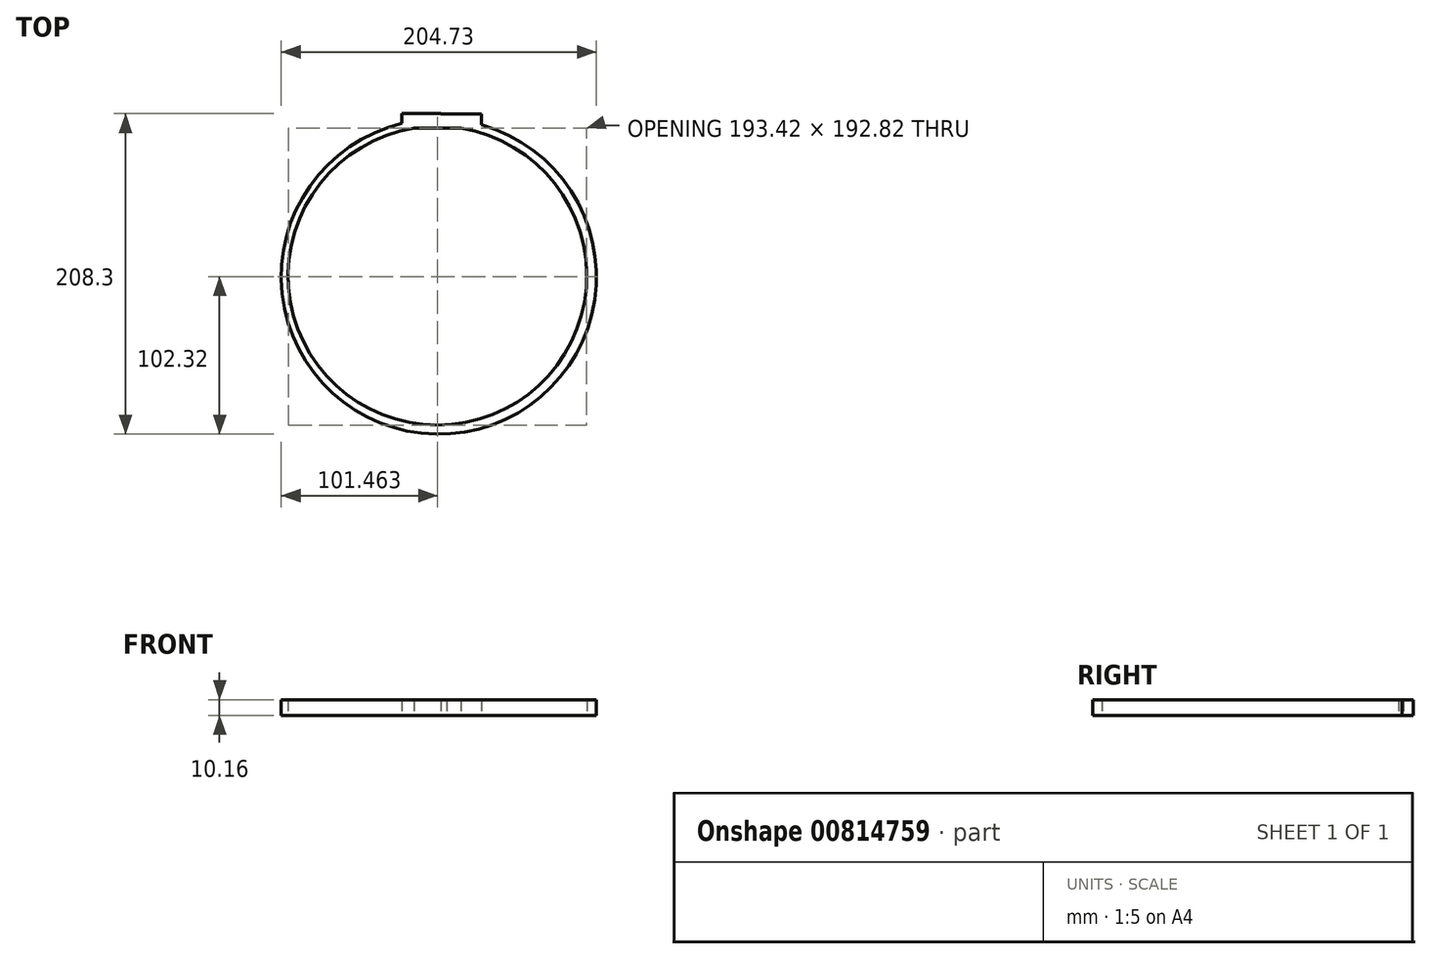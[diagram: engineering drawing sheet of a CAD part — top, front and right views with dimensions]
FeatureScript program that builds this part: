
annotation { "Feature Type Name" : "Feature", "Feature Type Description" : "" }
export const myFeature = defineFeature(function(context is Context, id is Id, definition is map)
    precondition{}
    {
        {
            var Q0;
            Q0=qCreatedBy(makeId("Top.planeOp"),FACE);
            var sketch = newSketch(context, id + "F0", { "sketchPlane" : qUnion([Q0])});
            skArc(sketch, "E0", {"start": v(-17.55, 47) * mm, "mid": v(-0.47, -156.44) * mm, "end": v(13, 47.27) * mm});
            skLineSegment(sketch, "E1.bottom", {"start": v(-17.55, 42.28) * mm, "end": v(13, 42.28) * mm});
            skLineSegment(sketch, "E1.top", {"start": v(-17.55, 51.72) * mm, "end": v(13, 51.72) * mm});
            skLineSegment(sketch, "E1.left", {"start": v(-17.55, 42.28) * mm, "end": v(-17.55, 51.72) * mm});
            skLineSegment(sketch, "E1.right", {"start": v(13, 42.28) * mm, "end": v(13, 51.72) * mm});
            skArc(sketch, "E2", {"start": v(-17.55, 42.28) * mm, "mid": v(-2.28, -150.54) * mm, "end": v(13, 42.28) * mm});
            skSolve(sketch);
        }
        {
            var Q0;
            Q0 = qSketchRegion(id + "F0", true);
            extrude(context, id + "F1", {"entities" : qUnion([Q0]), "depth" : 10.16 * mm, "offsetDistance" : 25.4 * mm});
        }
        {
            var Q0;
            Q0=qCreatedBy(makeId("Top.planeOp"),FACE);
            var sketch = newSketch(context, id + "F2", { "sketchPlane" : qUnion([Q0])});
            skLineSegment(sketch, "E3.bottom", {"start": v(3.85, 51.76) * mm, "end": v(26.3, 51.76) * mm});
            skLineSegment(sketch, "E3.top", {"start": v(3.85, 43.95) * mm, "end": v(26.3, 43.95) * mm});
            skLineSegment(sketch, "E3.left", {"start": v(3.85, 51.76) * mm, "end": v(3.85, 43.95) * mm});
            skLineSegment(sketch, "E3.right", {"start": v(26.3, 51.76) * mm, "end": v(26.3, 43.95) * mm});
            skLineSegment(sketch, "E4.bottom", {"start": v(0, 51.85) * mm, "end": v(-25.42, 51.85) * mm});
            skLineSegment(sketch, "E4.top", {"start": v(0, 43.95) * mm, "end": v(-25.42, 43.95) * mm});
            skLineSegment(sketch, "E4.left", {"start": v(0, 51.85) * mm, "end": v(0, 43.95) * mm});
            skLineSegment(sketch, "E4.right", {"start": v(-25.42, 51.85) * mm, "end": v(-25.42, 43.95) * mm});
            skSolve(sketch);
        }
        {
            var Q0;
            Q0 = qSketchRegion(id + "F2", true);
            extrude(context, id + "F3", {"entities" : qUnion([Q0]), "operationType" : NewBodyOperationType.ADD, "depth" : 10.16 * mm, "offsetDistance" : 25.4 * mm});
        }
    });
